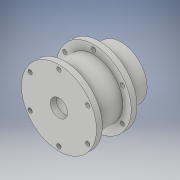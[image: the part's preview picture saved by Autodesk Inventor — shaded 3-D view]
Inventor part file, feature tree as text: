
AUTODESK INVENTOR PART (.ipt)
format: ipt  version: 2017 (Build 210142000, 142)  size: 181,760 bytes
history: native  units: in
note: dims shown in document units (in); Inventor stores cm internally (conversion verified against a paired STEP export)
features: sketch x9, extrude x8, other x2, loft x1, hole x1
ambient origin geometry x8: Origin, YZ Plane, XZ Plane, XY Plane, X Axis, Y Axis, Z Axis, Center Point
bodies: Solid1 (feature_tree)
feature tree (21):
  extrude  "Extrusion1"  Depth=2.68in TaperAngle=0.0deg
  extrude  "Extrusion2"  Depth=2.68in TaperAngle=0.0deg
  extrude  "Extrusion3"  Depth=0.93in TaperAngle=0.0deg
  extrude  "Extrusion4"  TaperAngle=0.0deg  [1 undecoded]
  loft  "Loft1"
  hole  "Hole1"  [1 undecoded]
  sketch  "Sketch6"  dims[d15=0.75in d16=1.65in d17=0.375in d18=0.25in d19=0.5635in d20=1.985in d21=0.8108in d22=2.5in]
  extrude  "Extrusion5"  Depth=0.25in TaperAngle=0.0deg
  extrude  "Extrusion6"  Depth=2.3622in TaperAngle=360.0deg
  extrude  "Extrusion7"  Depth=5.0in TaperAngle=0.0deg
  extrude  "Extrusion8"  [1 undecoded]
  sketch  "Sketch1"  dims[d0=3.24in d1=2.68in d2=0.0in]
  sketch  "Sketch2"  dims[d3=0.75in d4=2.68in d5=0.0in]
  sketch  "Sketch3"  dims[d6=1.72in d7=0.93in d8=0.0in]
  sketch  "Sketch4"  dims[d9=0.25in d10=0.0in d11=0.0in d12=90.0deg]
  other  "Edges1"
  other  "Edges2"
  sketch  "Sketch5"  dims[d13=0.0in d14=90.0deg]
  sketch  "Sketch7"  dims[d23=2.25in d24=0.93in d25=0.0in]
  sketch  "Sketch8"  dims[d26=1.5in d27=0.0in d28=0.25in d29=0.0in]
  sketch  "Sketch9"  dims[d30=0.1875in d31=2.3622in d33=360.0deg d35=5.0in d36=0.0in]
note: 3 required parameter values undecoded (feature->parameter linkage not recoverable at this tier; creation-order binding heuristic only, values carry confidence <= 0.55)
